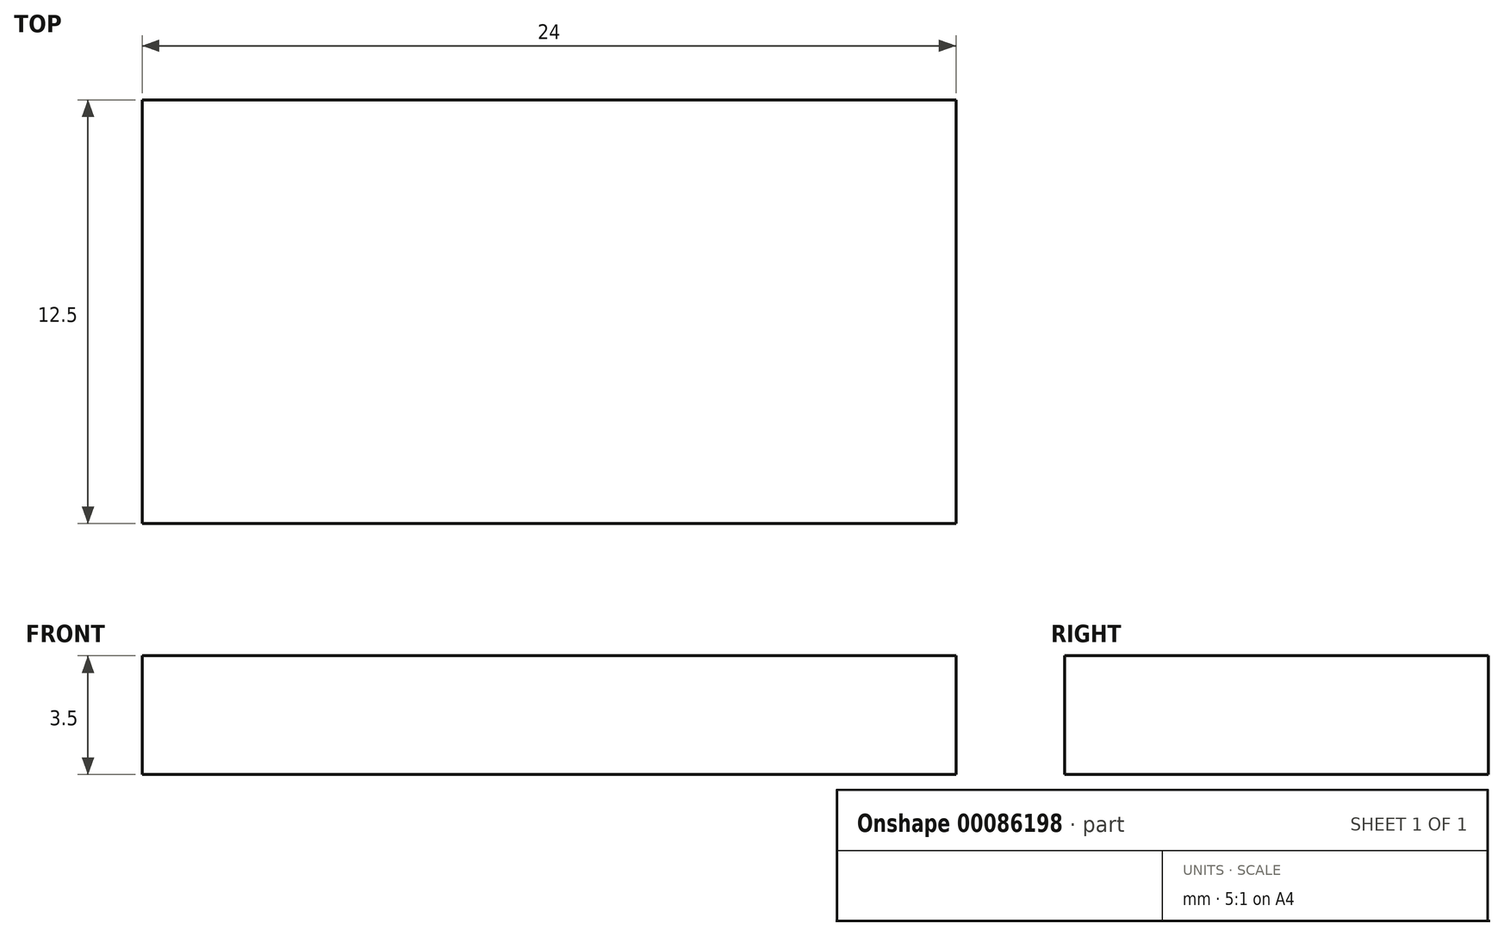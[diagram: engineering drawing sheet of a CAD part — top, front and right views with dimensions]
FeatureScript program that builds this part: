
annotation { "Feature Type Name" : "Feature", "Feature Type Description" : "" }
export const myFeature = defineFeature(function(context is Context, id is Id, definition is map)
    precondition{}
    {
        {
            var Q0;
            Q0=qCreatedBy(makeId("Top.planeOp"),FACE);
            var sketch = newSketch(context, id + "F0", { "sketchPlane" : qUnion([Q0])});
            skLineSegment(sketch, "E0.bottom", {"start": v(-14.5, 6.64) * mm, "end": v(9.5, 6.64) * mm});
            skLineSegment(sketch, "E0.top", {"start": v(-14.5, -5.86) * mm, "end": v(9.5, -5.86) * mm});
            skLineSegment(sketch, "E0.left", {"start": v(-14.5, 6.64) * mm, "end": v(-14.5, -5.86) * mm});
            skLineSegment(sketch, "E0.right", {"start": v(9.5, 6.64) * mm, "end": v(9.5, -5.86) * mm});
            skLineSegment(sketch, "E1.left", {"start": v(-14.5, 6.64) * mm, "end": v(-14.5, -4.36) * mm});
            skSolve(sketch);
        }
        {
            var Q0;
            {var subQ1=sQuery(id+"F0.wireOp",EDGE,"E0.right");Q0=makeQuery(id+"F0.imprint","IMPRINT",FACE,{"disambiguationData":[TD([[makeQuery(id+"F0.imprint","IMPRINT",EDGE,{"derivedFrom":subQ1}),-1.0]])]});}
            extrude(context, id + "F1", {"entities" : qUnion([Q0]), "depth" : 3.5 * mm});
        }
    });
